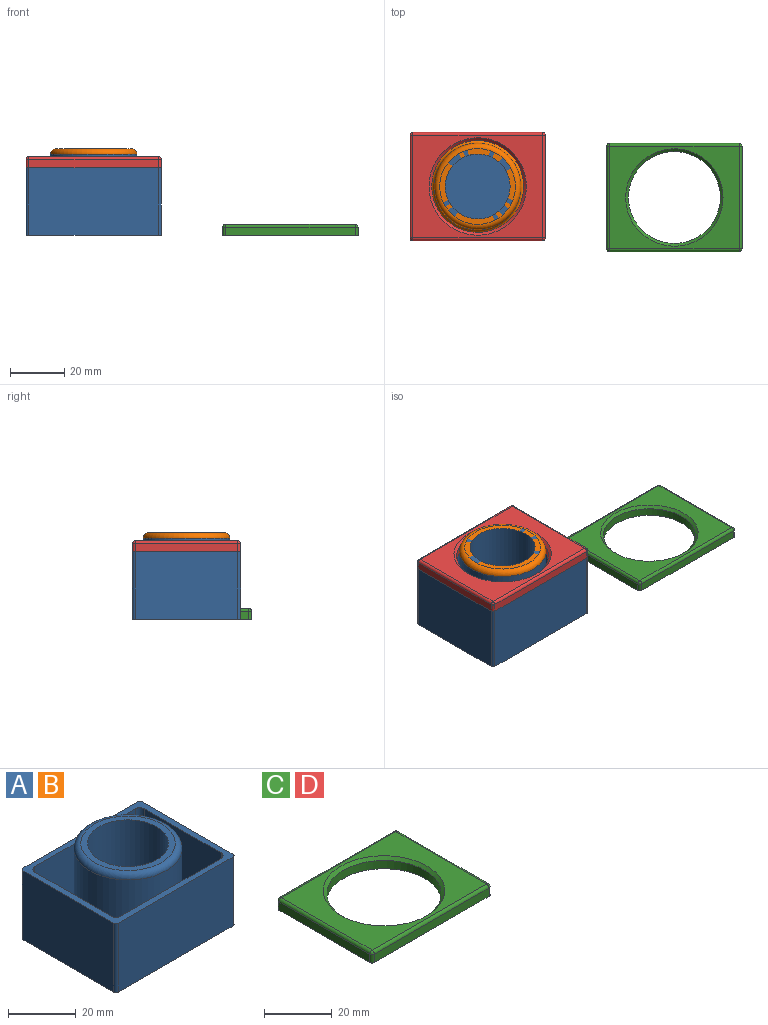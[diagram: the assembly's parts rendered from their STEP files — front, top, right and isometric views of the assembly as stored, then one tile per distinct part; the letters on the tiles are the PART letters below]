
ASSEMBLY  parts=4 mates=1
PART A: 26 faces, bbox 50x42x32 mm
  f0: plane 36x23mm, normal (0,0,1), area 317.3mm2, adj f8,f9,f10,f20,f23,f24
  f1: plane 50x40mm, normal (0,0,1), area 346.6mm2, adj f2,f3,f4,f5,f7,f8,f9,f10
  f2: plane 38x25mm, normal (-1,0,0), area 950mm2, adj f1,f6,f16,f19
  f3: plane 48x25mm, normal (0,-1,0), area 1200mm2, adj f1,f6,f16,f17
  f4: plane 38x25mm, normal (1,0,0), area 950mm2, adj f1,f6,f17,f18
  f5: plane 48x25mm, normal (0,1,0), area 1200mm2, adj f1,f6,f18,f19
  f6: plane 50x40mm, normal (0,0,-1), area 1999.1mm2, adj f2,f3,f4,f5,f16,f17,f18,f19
  f7: plane 32x23mm, normal (-1,0,0), area 736mm2, adj f1,f11,f22,f25
  f8: plane 42x23mm, normal (0,-1,0), area 966mm2, adj f0,f1,f11,f22,f23
  f9: plane 32x23mm, normal (1,0,0), area 736mm2, adj f0,f1,f23,f24
  f10: plane 42x23mm, normal (0,1,0), area 966mm2, adj f0,f1,f11,f24,f25
  f11: plane 36x23mm, normal (0,0,1), area 317.3mm2, adj f7,f8,f10,f20,f22,f25
  f12: cylinder r=16mm len=32mm, axis (0,0,-1), area 2613.8mm2, adj f20,f21
  f13: plane 28x28mm, normal (0,0,1), area 163.4mm2, adj f14,f21
  f14: cylinder r=12mm len=24mm, axis (0,0,1), area 1508mm2, adj f13,f15
  f15: plane 24x24mm, normal (0,0,1), area 452.4mm2, adj f14
  f16: cylinder r=1mm len=25mm, axis (0,0,1), area 39.3mm2, adj f1,f2,f3,f6
  f17: cylinder r=1mm len=25mm, axis (0,0,-1), area 39.3mm2, adj f1,f3,f4,f6
  f18: cylinder r=1mm len=25mm, axis (0,0,1), area 39.3mm2, adj f1,f4,f5,f6
  f19: cylinder r=1mm len=25mm, axis (0,0,-1), area 39.3mm2, adj f1,f2,f5,f6
  f20: torus R=18mm, axis (0,0,1), area 330.2mm2, adj f0,f11,f12
  f21: torus R=14mm, axis (0,0,1), area 301.5mm2, adj f12,f13
  f22: cylinder r=2mm len=23mm, axis (0,0,1), area 72.3mm2, adj f1,f7,f8,f11
  f23: cylinder r=2mm len=23mm, axis (0,0,-1), area 72.3mm2, adj f0,f1,f8,f9
  f24: cylinder r=2mm len=23mm, axis (0,0,1), area 72.3mm2, adj f0,f1,f9,f10
  f25: cylinder r=2mm len=23mm, axis (0,0,-1), area 72.3mm2, adj f1,f7,f10,f11
PART B: same geometry as A
PART C: 20 faces, bbox 50x40x4 mm
  f0: plane 38x3mm, normal (-1,0,0), area 114mm2, adj f5,f8,f12,f14
  f1: plane 48x3mm, normal (0,-1,0), area 144mm2, adj f5,f9,f14,f19
  f2: plane 38x3mm, normal (1,0,0), area 114mm2, adj f5,f11,f16,f19
  f3: plane 48x3mm, normal (0,1,0), area 144mm2, adj f5,f10,f12,f16
  f4: plane 48x38mm, normal (0,0,1), area 806.1mm2, adj f7,f8,f9,f10,f11
  f5: plane 50x40mm, normal (0,0,-1), area 1091.2mm2, adj f0,f1,f2,f3,f6,f12,f14,f16
  f6: cylinder r=17mm len=34mm, axis (0,0,1), area 320.4mm2, adj f5,f7
  f7: cone r=17mm half-angle=45deg, axis (0,0,1), area 155.5mm2, adj f4,f6
  f8: cylinder r=1mm len=38mm, axis (0,1,0), area 59.7mm2, adj f0,f4,f13,f15
  f9: cylinder r=1mm len=48mm, axis (-1,0,0), area 75.4mm2, adj f1,f4,f15,f18
  f10: cylinder r=1mm len=48mm, axis (1,0,0), area 75.4mm2, adj f3,f4,f13,f17
  f11: cylinder r=1mm len=38mm, axis (0,-1,0), area 59.7mm2, adj f2,f4,f17,f18
  f12: cylinder r=1mm len=3mm, axis (0,0,-1), area 4.7mm2, adj f0,f3,f5,f13
  f13: sphere r=1mm, area 1.6mm2, adj f8,f10,f12
  f14: cylinder r=1mm len=3mm, axis (0,0,1), area 4.7mm2, adj f0,f1,f5,f15
  f15: sphere r=1mm, area 1.6mm2, adj f8,f9,f14
  f16: cylinder r=1mm len=3mm, axis (0,0,1), area 4.7mm2, adj f2,f3,f5,f17
  f17: sphere r=1mm, area 1.6mm2, adj f10,f11,f16
  f18: sphere r=1mm, area 1.6mm2, adj f9,f11,f19
  f19: cylinder r=1mm len=3mm, axis (0,0,-1), area 4.7mm2, adj f1,f2,f5,f18
PART D: same geometry as C
PLACE A at identity fixed
PLACE B at identity
PLACE C at identity
PLACE D t=(-72.74,4.02,25)mm
MATE slider A.f16 <-> D.f14  axis (0,0,1) through (-60.76,-57.22,25)mm
